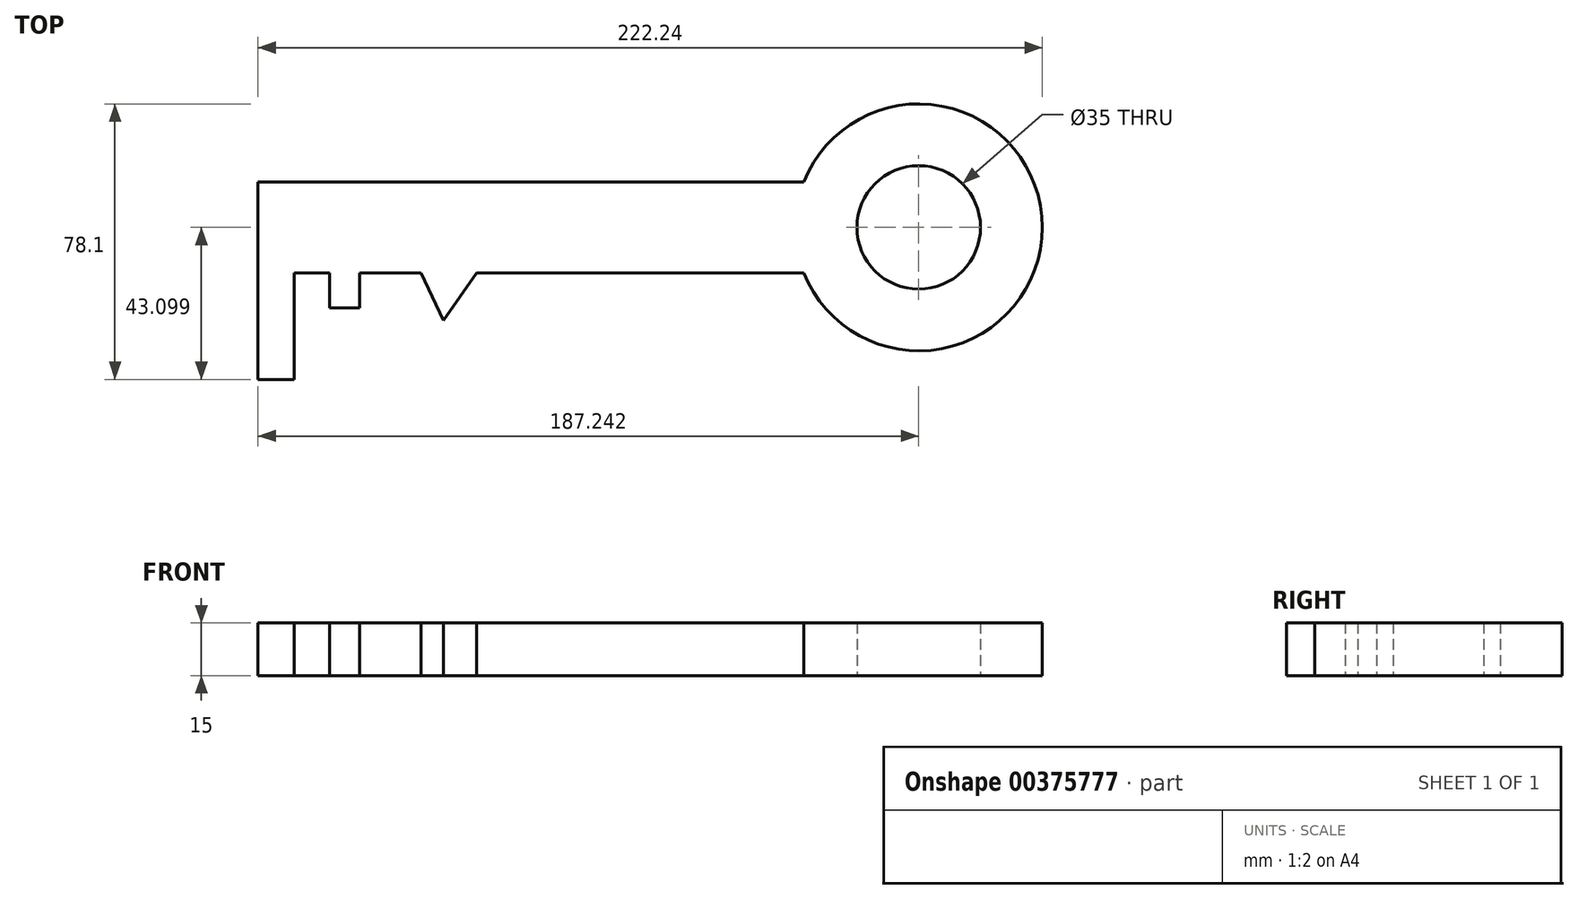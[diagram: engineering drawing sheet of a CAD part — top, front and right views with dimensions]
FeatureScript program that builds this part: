
annotation { "Feature Type Name" : "Feature", "Feature Type Description" : "" }
export const myFeature = defineFeature(function(context is Context, id is Id, definition is map)
    precondition{}
    {
        {
            var Q0;
            Q0=qCreatedBy(makeId("Top.planeOp"),FACE);
            var sketch = newSketch(context, id + "F0", { "sketchPlane" : qUnion([Q0])});
            skLineSegment(sketch, "E0.bottom", {"start": v(0, 0) * mm, "end": v(-92.7, 0) * mm});
            skLineSegment(sketch, "E0.top", {"start": v(0, 25.72) * mm, "end": v(-154.7, 25.72) * mm});
            skLineSegment(sketch, "E0.right", {"start": v(-154.7, 0) * mm, "end": v(-154.7, 25.72) * mm});
            skLineSegment(sketch, "E1.top", {"start": v(-154.7, -30.24) * mm, "end": v(-144.36, -30.24) * mm});
            skLineSegment(sketch, "E1.left", {"start": v(-154.7, 0) * mm, "end": v(-154.7, -30.24) * mm});
            skLineSegment(sketch, "E1.right", {"start": v(-144.36, 0) * mm, "end": v(-144.36, -30.24) * mm});
            skLineSegment(sketch, "E2.top", {"start": v(-134.36, -10) * mm, "end": v(-125.85, -10) * mm});
            skLineSegment(sketch, "E2.left", {"start": v(-134.36, 0) * mm, "end": v(-134.36, -10) * mm});
            skLineSegment(sketch, "E2.right", {"start": v(-125.85, 0) * mm, "end": v(-125.85, -10) * mm});
            skLineSegment(sketch, "E3", {"start": v(-108.5, 0) * mm, "end": v(-102.11, -13.52) * mm});
            skLineSegment(sketch, "E4", {"start": v(-102.11, -13.52) * mm, "end": v(-92.7, 0) * mm});
            skArc(sketch, "E5", {"start": v(0, 0) * mm, "mid": v(67.55, 12.86) * mm, "end": v(0, 25.72) * mm});
            skCircle(sketch, "E6", {"center": v(32.55, 12.86) * mm, "radius": 17.5 * mm});
            skLineSegment(sketch, "E7.trimOffspring", {"start": v(-108.5, 0) * mm, "end": v(-125.85, 0) * mm});
            skLineSegment(sketch, "E8.trimOffspring", {"start": v(-134.36, 0) * mm, "end": v(-144.36, 0) * mm});
            skSolve(sketch);
        }
        {
            var Q0;
            Q0 = qSketchRegion(id + "F0", true);
            extrude(context, id + "F1", {"entities" : qUnion([Q0]), "depth" : 15 * mm});
        }
    });
